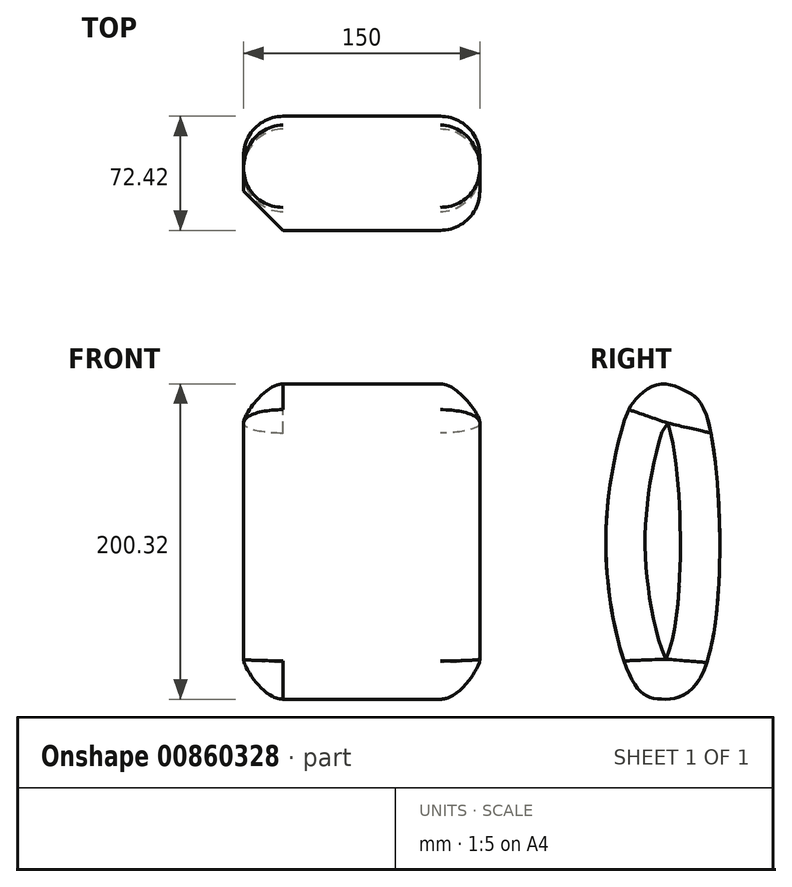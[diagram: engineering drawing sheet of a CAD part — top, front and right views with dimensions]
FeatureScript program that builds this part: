
annotation { "Feature Type Name" : "Feature", "Feature Type Description" : "" }
export const myFeature = defineFeature(function(context is Context, id is Id, definition is map)
    precondition{}
    {
        {
            var Q0;
            Q0=qCreatedBy(makeId("Right.planeOp"),FACE);
            var sketch = newSketch(context, id + "F0", { "sketchPlane" : qUnion([Q0])});
            skFitSpline(sketch, "E0", {"points": [v(0, 0) * mm, v(-16.64, -11.52) * mm, v(-23.17, -25.87) * mm, v(-34.25, -99.56) * mm, v(-15.34, -191.52) * mm, v(0, -200) * mm, v(26.24, -185.79) * mm, v(30.3, -21.88) * mm, v(17.02, -4.7) * mm, v(0, 0) * mm]});
            skLineSegment(sketch, "E1", {"start": v(0, 0) * mm, "end": v(0, -200) * mm, "construction": true});
            skSolve(sketch);
        }
        {
            var Q0;
            Q0 = qSketchRegion(id + "F0", true);
            extrude(context, id + "F1", {"entities" : qUnion([Q0]), "depth" : 150 * mm, "offsetDistance" : 25 * mm});
        }
        {
            var Q0;
            Q0=makeQuery(id+"F1.opExtrude","CAP_EDGE",EDGE,{"disambiguationData":[OSD([sQuery(id+"F0.wireOp",EDGE,"E0")])],"isStart":false});
            var Q1;
            Q1=makeQuery(id+"F1.opExtrude","CAP_EDGE",EDGE,{"disambiguationData":[OSD([sQuery(id+"F0.wireOp",EDGE,"E0")])],"isStart":true});
            fillet(context, id + "F2", {"entities" : qUnion([Q0, Q1]), "radius" : 25 * mm, "tangentPropagation" : true, "allowEdgeOverflow" : false});
        }
    });
